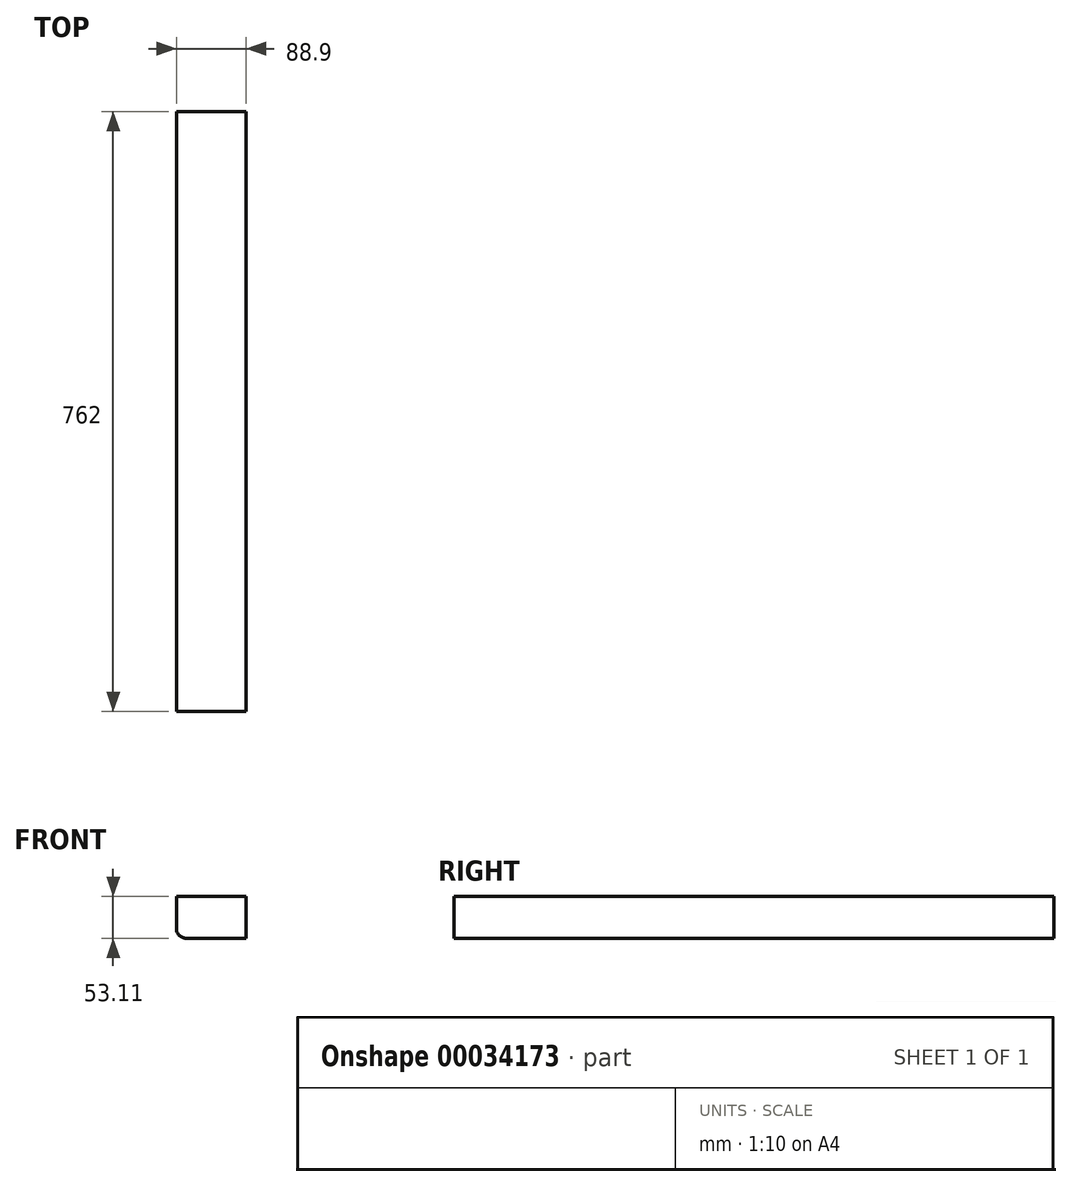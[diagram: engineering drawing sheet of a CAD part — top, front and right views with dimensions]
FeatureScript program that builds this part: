
annotation { "Feature Type Name" : "Feature", "Feature Type Description" : "" }
export const myFeature = defineFeature(function(context is Context, id is Id, definition is map)
    precondition{}
    {
        {
            var Q0;
            Q0=qCreatedBy(makeId("Top.planeOp"),FACE);
            var sketch = newSketch(context, id + "F0", { "sketchPlane" : qUnion([Q0])});
            skLineSegment(sketch, "E0.bottom", {"start": v(0, 762) * mm, "end": v(-88.9, 762) * mm});
            skLineSegment(sketch, "E0.top", {"start": v(0, 0) * mm, "end": v(-88.9, 0) * mm});
            skLineSegment(sketch, "E0.left", {"start": v(0, 762) * mm, "end": v(0, 0) * mm});
            skLineSegment(sketch, "E0.right", {"start": v(-88.9, 762) * mm, "end": v(-88.9, 0) * mm});
            skLineSegment(sketch, "E1", {"start": v(0, -622.76) * mm, "end": v(0, 637.95) * mm, "construction": true});
            skLineSegment(sketch, "E2.MirrorCS", {"start": v(88.9, 762) * mm, "end": v(88.9, 0) * mm});
            skLineSegment(sketch, "E3.MirrorCS", {"start": v(0, 762) * mm, "end": v(88.9, 762) * mm});
            skSolve(sketch);
        }
        {
            var Q0;
            Q0=qCreatedBy(makeId("Top.planeOp"),FACE);
            var sketch = newSketch(context, id + "F1", { "sketchPlane" : qUnion([Q0])});
            skFitSpline(sketch, "E4", {"points": [v(-88.6, 0) * mm, v(-86.12, -42.2) * mm, v(-72.02, -115.38) * mm, v(-50.47, -168.24) * mm, v(0, -279.44) * mm], "startDerivative": vector(5.05, -174.6) * mm, "endDerivative": vector(123.7, -240.4) * mm});
            skFitSpline(sketch, "E5.MirrorCS", {"points": [v(88.6, 0) * mm, v(86.12, -42.2) * mm, v(72.02, -115.38) * mm, v(50.47, -168.24) * mm, v(0, -279.44) * mm], "startDerivative": vector(-5.05, -174.6) * mm, "endDerivative": vector(-123.7, -240.4) * mm});
            skSolve(sketch);
        }
        {
            var Q0;
            Q0 = qSketchRegion(id + "F0", true);
            var Q1;
            Q1 = qSketchRegion(id + "F1", true);
            extrude(context, id + "F2", {"entities" : qUnion([Q0, Q1]), "depth" : 53.1 * mm});
        }
        {
            var Q0;
            Q0=makeQuery(id+"F2.opExtrude","CAP_EDGE",EDGE,{"disambiguationData":[OSD([sQuery(id+"F0.wireOp",EDGE,"E0.right")])],"isStart":true});
            fillet(context, id + "F3", {"entities" : qUnion([Q0]), "radius" : 12.7 * mm, "tangentPropagation" : true, "allowEdgeOverflow" : false});
        }
    });
